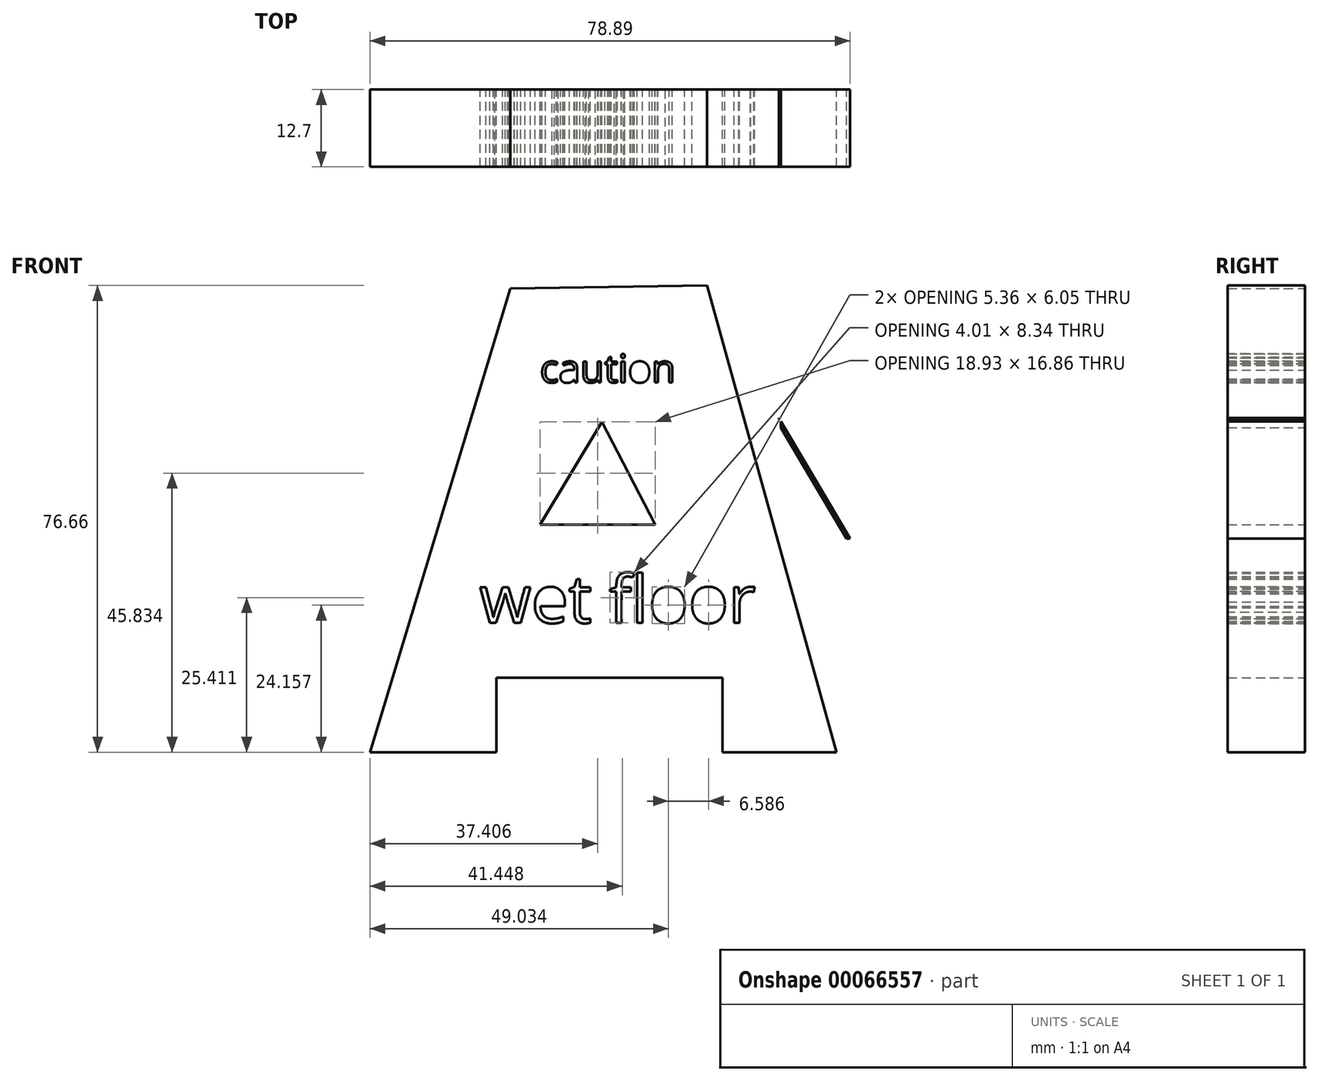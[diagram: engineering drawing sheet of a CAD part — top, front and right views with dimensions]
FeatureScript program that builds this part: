
annotation { "Feature Type Name" : "Feature", "Feature Type Description" : "" }
export const myFeature = defineFeature(function(context is Context, id is Id, definition is map)
    precondition{}
    {
        {
            var Q0;
            Q0=qCreatedBy(makeId("Front.planeOp"),FACE);
            var sketch = newSketch(context, id + "F0", { "sketchPlane" : qUnion([Q0])});
            skLineSegment(sketch, "E0", {"start": v(0, 35.21) * mm, "end": v(-11.31, 35.21) * mm});
            skLineSegment(sketch, "E1", {"start": v(-11.31, 35.21) * mm, "end": v(1.61, 35.21) * mm});
            skLineSegment(sketch, "E2", {"start": v(1.61, 35.21) * mm, "end": v(27.94, -9.35) * mm});
            skLineSegment(sketch, "E3", {"start": v(27.94, -9.35) * mm, "end": v(16.16, -9.35) * mm});
            skLineSegment(sketch, "E4", {"start": v(16.16, -9.35) * mm, "end": v(12.47, 0) * mm});
            skLineSegment(sketch, "E5", {"start": v(12.47, 0) * mm, "end": v(0, 0) * mm});
            skLineSegment(sketch, "E6", {"start": v(0, 0) * mm, "end": v(-10.16, 0) * mm});
            skLineSegment(sketch, "E7", {"start": v(-10.16, 0) * mm, "end": v(-12.47, -8.9) * mm});
            skLineSegment(sketch, "E8", {"start": v(-12.47, -8.9) * mm, "end": v(-24.01, -8.9) * mm});
            skLineSegment(sketch, "E9", {"start": v(-24.01, -8.9) * mm, "end": v(-11.31, 35.21) * mm});
            skLineSegment(sketch, "E10", {"start": v(-8.5, 31.75) * mm, "end": v(-16.55, 3.78) * mm});
            skLineSegment(sketch, "E11", {"start": v(-16.55, 3.78) * mm, "end": v(19.6, 3.78) * mm});
            skLineSegment(sketch, "E12", {"start": v(19.6, 3.78) * mm, "end": v(2.66, 32.44) * mm});
            skLineSegment(sketch, "E13", {"start": v(2.66, 32.44) * mm, "end": v(-8.5, 31.75) * mm});
            skText(sketch, "E14", { "text": "caution", "fontName": "OpenSans-Regular.ttf"});
            skText(sketch, "E15", { "text": "wet", "fontName": "OpenSans-Regular.ttf"});
            const initialGuessF0  = {"E14": [-0.0073, 0.02619, 1, 0, 0.0029], "E15": [-0.07325, -0.0142, 1, 0, 0.06313]};
            skSetInitialGuess(sketch, initialGuessF0);
            skSolve(sketch);
        }
        {
            var Q0;
            {var subQ2=sQuery(id+"F0.wireOp",EDGE,"E2");Q0=makeQuery(id+"F0.imprint","IMPRINT",FACE,{"disambiguationData":[TD([[makeQuery(id+"F0.imprint","IMPRINT",EDGE,{"derivedFrom":subQ2}),-1.0]])]});}
            var Q1;
            Q1=makeQuery(id+"F0.imprint","IMPRINT",FACE,{"disambiguationData":[TD([[makeQuery(id+"F0.imprint","IMPRINT",EDGE,{"derivedFrom":sQuery(id+"F0.wireOp",EDGE,"WldrTsSC-c8Xf-BFZF-sgNJ-E7E4i1rRAhrD")}),1.0]])]});
            extrude(context, id + "F1", {"entities" : qUnion([Q0, Q1]), "depth" : 12.7 * mm});
        }
        {
            var Q0;
            Q0=qCreatedBy(makeId("Front.planeOp"),FACE);
            var sketch = newSketch(context, id + "F2", { "sketchPlane" : qUnion([Q0])});
            skLineSegment(sketch, "E16", {"start": v(-38.1, 49.07) * mm, "end": v(-61.2, -27.13) * mm});
            skLineSegment(sketch, "E17", {"start": v(-61.2, -27.13) * mm, "end": v(-40.4, -27.13) * mm});
            skLineSegment(sketch, "E18", {"start": v(-40.4, -27.13) * mm, "end": v(-40.4, -14.9) * mm});
            skLineSegment(sketch, "E19", {"start": v(-40.4, -14.9) * mm, "end": v(-3.23, -14.9) * mm});
            skLineSegment(sketch, "E20", {"start": v(-3.23, -14.9) * mm, "end": v(-3.23, -27.13) * mm});
            skLineSegment(sketch, "E21", {"start": v(-3.23, -27.13) * mm, "end": v(15.47, -27.13) * mm});
            skLineSegment(sketch, "E22", {"start": v(15.47, -27.13) * mm, "end": v(-5.77, 49.53) * mm});
            skLineSegment(sketch, "E23", {"start": v(-5.77, 49.53) * mm, "end": v(-38.1, 49.07) * mm});
            skLineSegment(sketch, "E24", {"start": v(-38.1, 43.3) * mm, "end": v(-7.4, 43.73) * mm});
            skLineSegment(sketch, "E25", {"start": v(-7.4, 43.73) * mm, "end": v(4.85, -7.97) * mm});
            skLineSegment(sketch, "E26", {"start": v(4.85, -7.97) * mm, "end": v(-47.34, -7.97) * mm});
            skLineSegment(sketch, "E27", {"start": v(-47.34, -7.97) * mm, "end": v(-38.1, 43.3) * mm});
            skText(sketch, "E28", { "text": "caution", "fontName": "OpenSans-Regular.ttf"});
            skText(sketch, "E29", { "text": "wet floor", "fontName": "OpenSans-Regular.ttf"});
            skLineSegment(sketch, "E30", {"start": v(-23.1, 27.13) * mm, "end": v(-33.25, 10.28) * mm});
            skLineSegment(sketch, "E31", {"start": v(-33.25, 10.28) * mm, "end": v(-14.32, 10.28) * mm});
            skLineSegment(sketch, "E32", {"start": v(-14.32, 10.28) * mm, "end": v(-23.1, 27.13) * mm});
            skCircle(sketch, "E33", {"center": v(-24.25, 18.7) * mm, "radius": 1.86 * mm});
            skPoint(sketch, "E33.centerSnap0", {"position": v(-18.7, 18.7) * mm});
            skLineSegment(sketch, "E34", {"start": v(-24.25, 18.7) * mm, "end": v(-24.25, 14.2) * mm});
            skLineSegment(sketch, "E35", {"start": v(-24.25, 14.2) * mm, "end": v(-20.32, 14.2) * mm});
            skLineSegment(sketch, "E36", {"start": v(-20.32, 14.2) * mm, "end": v(-20.32, 10.28) * mm});
            skLineSegment(sketch, "E37", {"start": v(-20.32, 10.28) * mm, "end": v(-20.32, 14.2) * mm});
            skLineSegment(sketch, "E38", {"start": v(-24.25, 14.2) * mm, "end": v(-28.63, 10.28) * mm});
            skLineSegment(sketch, "E39", {"start": v(-28.63, 10.28) * mm, "end": v(-24.25, 14.2) * mm});
            skLineSegment(sketch, "E40", {"start": v(-24.25, 14.2) * mm, "end": v(-29.12, 17.14) * mm});
            skLineSegment(sketch, "E41", {"start": v(-29.12, 17.14) * mm, "end": v(-24.25, 14.2) * mm});
            skLineSegment(sketch, "E42", {"start": v(-24.25, 14.2) * mm, "end": v(-20.32, 16.24) * mm});
            skLineSegment(sketch, "E43", {"start": v(-20.32, 16.24) * mm, "end": v(-22.38, 18.66) * mm});
            const initialGuessF2  = {"E28": [-0.03325, 0.0336, 1, 0, 0.00462], "E29": [-0.04318, -0.00589, 1, 0, 0.00785]};
            skSetInitialGuess(sketch, initialGuessF2);
            skSolve(sketch);
        }
        {
            var Q0;
            Q0=makeQuery(id+"F2.imprint","IMPRINT",FACE,{"disambiguationData":[TD([[makeQuery(id+"F2.imprint","IMPRINT",EDGE,{"derivedFrom":sQuery(id+"F2.wireOp",EDGE,"E16")}),1.0]])]});
            var Q1;
            Q1=makeQuery(id+"F2.imprint","IMPRINT",FACE,{"disambiguationData":[TD([[makeQuery(id+"F2.imprint","IMPRINT",EDGE,{"derivedFrom":sQuery(id+"F2.wireOp",EDGE,"E24")}),-1.0]])]});
            extrude(context, id + "F3", {"entities" : qUnion([Q0, Q1]), "depth" : 12.7 * mm});
        }
    });
